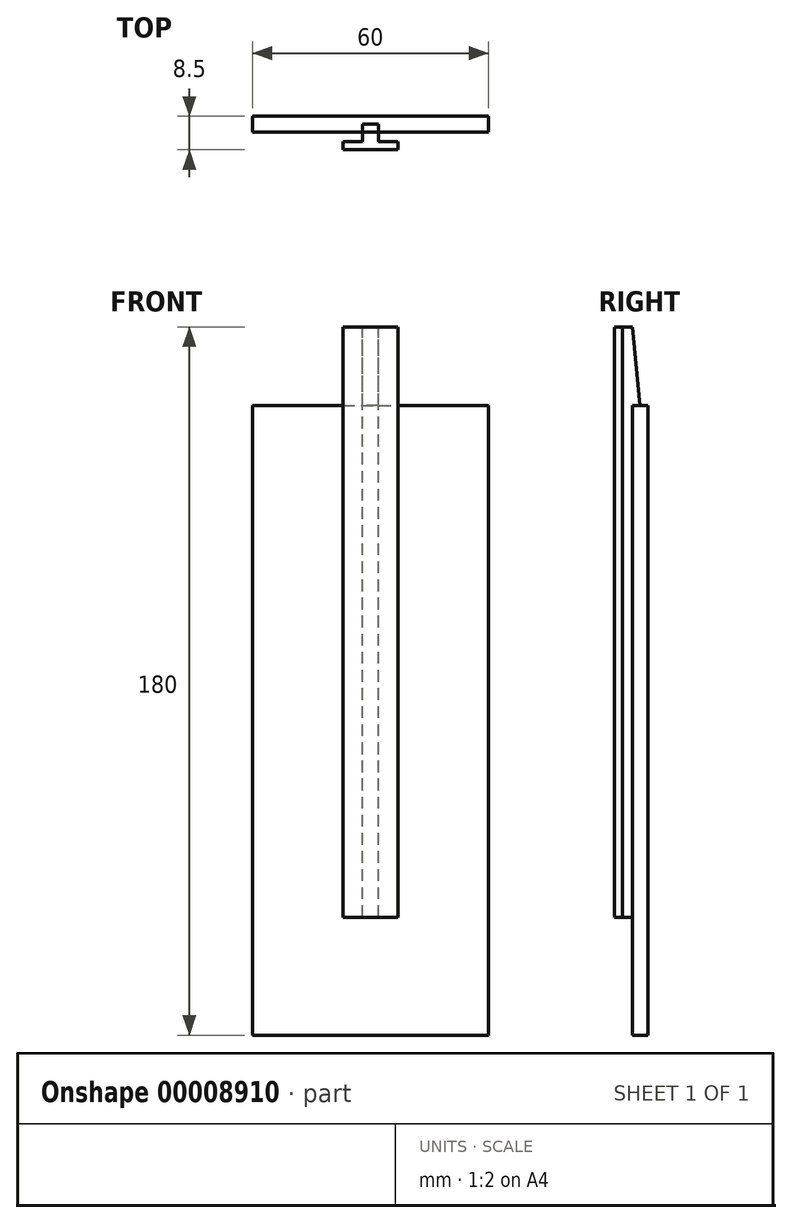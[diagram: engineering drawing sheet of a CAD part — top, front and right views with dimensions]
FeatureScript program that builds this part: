
annotation { "Feature Type Name" : "Feature", "Feature Type Description" : "" }
export const myFeature = defineFeature(function(context is Context, id is Id, definition is map)
    precondition{}
    {
        {
            var Q0;
            Q0=qCreatedBy(makeId("Front.planeOp"),FACE);
            var sketch = newSketch(context, id + "F0", { "sketchPlane" : qUnion([Q0])});
            skLineSegment(sketch, "E0", {"start": v(0, 0) * mm, "end": v(30, 0) * mm, "construction": true});
            skLineSegment(sketch, "E1", {"start": v(0, 0) * mm, "end": v(-30, 0) * mm, "construction": true});
            skLineSegment(sketch, "E2.0", {"start": v(0, -80) * mm, "end": v(30, -80) * mm});
            skLineSegment(sketch, "E3.0", {"start": v(0, -80) * mm, "end": v(-30, -80) * mm});
            skLineSegment(sketch, "E4.0", {"start": v(0, 80) * mm, "end": v(30, 80) * mm});
            skLineSegment(sketch, "E5.0", {"start": v(0, 80) * mm, "end": v(-30, 80) * mm});
            skLineSegment(sketch, "E6.0", {"start": v(30, 80) * mm, "end": v(30, -80) * mm});
            skLineSegment(sketch, "E7.0", {"start": v(-30, 80) * mm, "end": v(-30, -80) * mm});
            skSolve(sketch);
        }
        {
            var Q0;
            Q0=makeQuery(id+"F0.imprint","IMPRINT",FACE,{"disambiguationData":[TD([[makeQuery(id+"F0.imprint","IMPRINT",EDGE,{"derivedFrom":sQuery(id+"F0.wireOp",EDGE,"E2.0")}),1.0]])]});
            extrude(context, id + "F1", {"entities" : qUnion([Q0]), "oppositeDirection" : true, "depth" : 4 * mm});
        }
        {
            var Q0;
            Q0=makeQuery(id+"F1.opExtrude","SWEPT_FACE",FACE,{"disambiguationData":[OSD([sQuery(id+"F0.wireOp",EDGE,"E4.0"),sQuery(id+"F0.wireOp",EDGE,"E5.0")])]});
            var sketch = newSketch(context, id + "F2", { "sketchPlane" : qUnion([Q0])});
            skLineSegment(sketch, "E8.0", {"start": v(-2.5, 0) * mm, "end": v(-2.5, -2) * mm});
            skLineSegment(sketch, "E9.0", {"start": v(2.5, 0) * mm, "end": v(2.5, -2) * mm});
            skLineSegment(sketch, "E10.0", {"start": v(-7.5, -2) * mm, "end": v(-7.5, -5) * mm});
            skLineSegment(sketch, "E11.0", {"start": v(7.5, -2) * mm, "end": v(7.5, -5) * mm});
            skLineSegment(sketch, "E12.0", {"start": v(-2.5, -2) * mm, "end": v(-7.5, -2) * mm});
            skLineSegment(sketch, "E13.0", {"start": v(7.5, -2) * mm, "end": v(2.5, -2) * mm});
            skLineSegment(sketch, "E14.0", {"start": v(-2.5, -5) * mm, "end": v(-7.5, -5) * mm});
            skLineSegment(sketch, "E15.0", {"start": v(7.5, -5) * mm, "end": v(2.5, -5) * mm});
            skLineSegment(sketch, "E16", {"start": v(-2.5, -5) * mm, "end": v(2.5, -5) * mm});
            skLineSegment(sketch, "E17.0", {"start": v(-2, 0) * mm, "end": v(-2, -2.5) * mm});
            skLineSegment(sketch, "E18.0", {"start": v(2, 0) * mm, "end": v(2, -2.5) * mm});
            skLineSegment(sketch, "E19.0", {"start": v(7, -2.5) * mm, "end": v(2, -2.5) * mm});
            skLineSegment(sketch, "E19.1", {"start": v(7, -2.5) * mm, "end": v(7, -4.5) * mm});
            skLineSegment(sketch, "E19.2", {"start": v(7, -4.5) * mm, "end": v(2.5, -4.5) * mm});
            skLineSegment(sketch, "E19.3", {"start": v(-2.5, -4.5) * mm, "end": v(2.5, -4.5) * mm});
            skLineSegment(sketch, "E19.4", {"start": v(-2.5, -4.5) * mm, "end": v(-7, -4.5) * mm});
            skLineSegment(sketch, "E19.5", {"start": v(-7, -2.5) * mm, "end": v(-7, -4.5) * mm});
            skLineSegment(sketch, "E19.6", {"start": v(-2, -2.5) * mm, "end": v(-7, -2.5) * mm});
            skSolve(sketch);
        }
        {
            var Q0;
            {var subQ2=sQuery(id+"F2.wireOp",EDGE,"E17.0");Q0=makeQuery(id+"F2.imprint","IMPRINT",FACE,{"disambiguationData":[TD([[makeQuery(id+"F2.imprint","IMPRINT",EDGE,{"derivedFrom":subQ2}),1.0]])]});}
            extrude(context, id + "F3", {"entities" : qUnion([Q0]), "operationType" : NewBodyOperationType.ADD, "oppositeDirection" : true, "depth" : 60 * mm});
        }
        {
            var Q0;
            Q0=makeQuery(id+"F1.opExtrude","CAP_FACE",FACE,{"disambiguationData":[OSD([sQuery(id+"F0.wireOp",EDGE,"E2.0"),sQuery(id+"F0.wireOp",EDGE,"E3.0"),sQuery(id+"F0.wireOp",EDGE,"E4.0"),sQuery(id+"F0.wireOp",EDGE,"E5.0"),sQuery(id+"F0.wireOp",EDGE,"c716fc53-c32f-4a1b-9b4a-c1987d26916d"),sQuery(id+"F0.wireOp",EDGE,"9a133eae-92d4-40d1-8971-3d120b290b95")])],"isStart":false});
            var sketch = newSketch(context, id + "F4", { "sketchPlane" : qUnion([Q0])});
            skLineSegment(sketch, "E20.0", {"start": v(-32, 43) * mm, "end": v(-32, -43) * mm});
            skLineSegment(sketch, "E21.0", {"start": v(27, 85) * mm, "end": v(-27, 85) * mm});
            skSolve(sketch);
        }
        {
            var Q0;
            Q0=makeQuery(id+"F3.opExtrude","SWEPT_FACE",FACE,{"disambiguationData":[OSD([sQuery(id+"F2.wireOp",EDGE,"E19.2"),sQuery(id+"F2.wireOp",EDGE,"E19.3"),sQuery(id+"F2.wireOp",EDGE,"E19.4")])]});
            var sketch = newSketch(context, id + "F5", { "sketchPlane" : qUnion([Q0])});
            skLineSegment(sketch, "E22", {"start": v(-7, 80) * mm, "end": v(-7, 20) * mm});
            skSolve(sketch);
        }
        {
            var Q0;
            Q0 = qSketchRegion(id + "F5", true);
            var Q1;
            Q1=makeQuery(id+"F3.opExtrude","CAP_FACE",FACE,{"disambiguationData":[OSD([sQuery(id+"F0.wireOp",EDGE,"E4.0"),sQuery(id+"F0.wireOp",EDGE,"E5.0"),sQuery(id+"F2.wireOp",EDGE,"E17.0"),sQuery(id+"F2.wireOp",EDGE,"E18.0"),sQuery(id+"F2.wireOp",EDGE,"E19.0"),sQuery(id+"F2.wireOp",EDGE,"E19.1"),sQuery(id+"F2.wireOp",EDGE,"E19.2"),sQuery(id+"F2.wireOp",EDGE,"E19.3"),sQuery(id+"F2.wireOp",EDGE,"E19.4"),sQuery(id+"F2.wireOp",EDGE,"E19.5"),sQuery(id+"F2.wireOp",EDGE,"E19.6")])],"isStart":false});
            extrude(context, id + "F6", {"entities" : qUnion([Q0, Q1]), "operationType" : NewBodyOperationType.ADD, "depth" : 70 * mm});
        }
        {
            var Q0;
            Q0=makeQuery(id+"F4.imprint","IMPRINT",FACE,{"disambiguationData":[TD([[makeQuery(id+"F4.imprint","IMPRINT",EDGE,{"derivedFrom":makeQuery(id+"F1.opExtrude","CAP_EDGE",EDGE,{"disambiguationData":[OSD([sQuery(id+"F0.wireOp",EDGE,"E6.0")])],"isStart":false})}),1.0]])]});
            var sketch = newSketch(context, id + "F7", { "sketchPlane" : qUnion([Q0])});
            skLineSegment(sketch, "E23.0", {"start": v(-35, 80) * mm, "end": v(-35, -80) * mm});
            skSolve(sketch);
        }
        {
            var Q0;
            {var subQ0=sQuery(id+"F0.wireOp",EDGE,"E4.0");var subQ1=sQuery(id+"F0.wireOp",EDGE,"E5.0");Q0=makeQuery(id+"F3.boolean.opBoolean","MERGE",FACE,{"derivedFrom":[makeQuery(id+"F1.opExtrude","SWEPT_FACE",FACE,{"disambiguationData":[OSD([subQ0,subQ1])]}),makeQuery(id+"F3.opExtrude","CAP_FACE",FACE,{"disambiguationData":[OSD([subQ0,subQ1,sQuery(id+"F2.wireOp",EDGE,"E17.0"),sQuery(id+"F2.wireOp",EDGE,"E18.0"),sQuery(id+"F2.wireOp",EDGE,"E19.0"),sQuery(id+"F2.wireOp",EDGE,"E19.1"),sQuery(id+"F2.wireOp",EDGE,"E19.2"),sQuery(id+"F2.wireOp",EDGE,"E19.3"),sQuery(id+"F2.wireOp",EDGE,"E19.4"),sQuery(id+"F2.wireOp",EDGE,"E19.5"),sQuery(id+"F2.wireOp",EDGE,"E19.6")])],"isStart":true})]});}
            var sketch = newSketch(context, id + "F8", { "sketchPlane" : qUnion([Q0])});
            skLineSegment(sketch, "E24", {"start": v(-2, 0) * mm, "end": v(2, 0) * mm});
            skSolve(sketch);
        }
        {
            var Q0;
            Q0=makeQuery(id+"F8.imprint","IMPRINT",FACE,{"disambiguationData":[TD([[makeQuery(id+"F8.imprint","IMPRINT",EDGE,{"derivedFrom":sQuery(id+"F8.wireOp",EDGE,"E24")}),-1.0]])]});
            extrude(context, id + "F9", {"entities" : qUnion([Q0]), "operationType" : NewBodyOperationType.ADD, "depth" : 20 * mm});
        }
        {
            var Q0;
            Q0=qCreatedBy(makeId("Right.planeOp"),FACE);
            var sketch = newSketch(context, id + "F10", { "sketchPlane" : qUnion([Q0])});
            skLineSegment(sketch, "E25", {"start": v(2, 80) * mm, "end": v(0, 100) * mm});
            skLineSegment(sketch, "E26", {"start": v(0, 100) * mm, "end": v(0, 80) * mm});
            skLineSegment(sketch, "E27", {"start": v(0, 80) * mm, "end": v(2, 80) * mm});
            skSolve(sketch);
        }
        {
            var Q0;
            Q0=makeQuery(id+"F10.imprint","IMPRINT",FACE,{"disambiguationData":[TD([[makeQuery(id+"F10.imprint","IMPRINT",EDGE,{"derivedFrom":sQuery(id+"F10.wireOp",EDGE,"E25")}),1.0]])]});
            extrude(context, id + "F11", {"entities" : qUnion([Q0]), "operationType" : NewBodyOperationType.ADD, "endBound" : BoundingType.SYMMETRIC, "depth" : 4 * mm});
        }
    });
